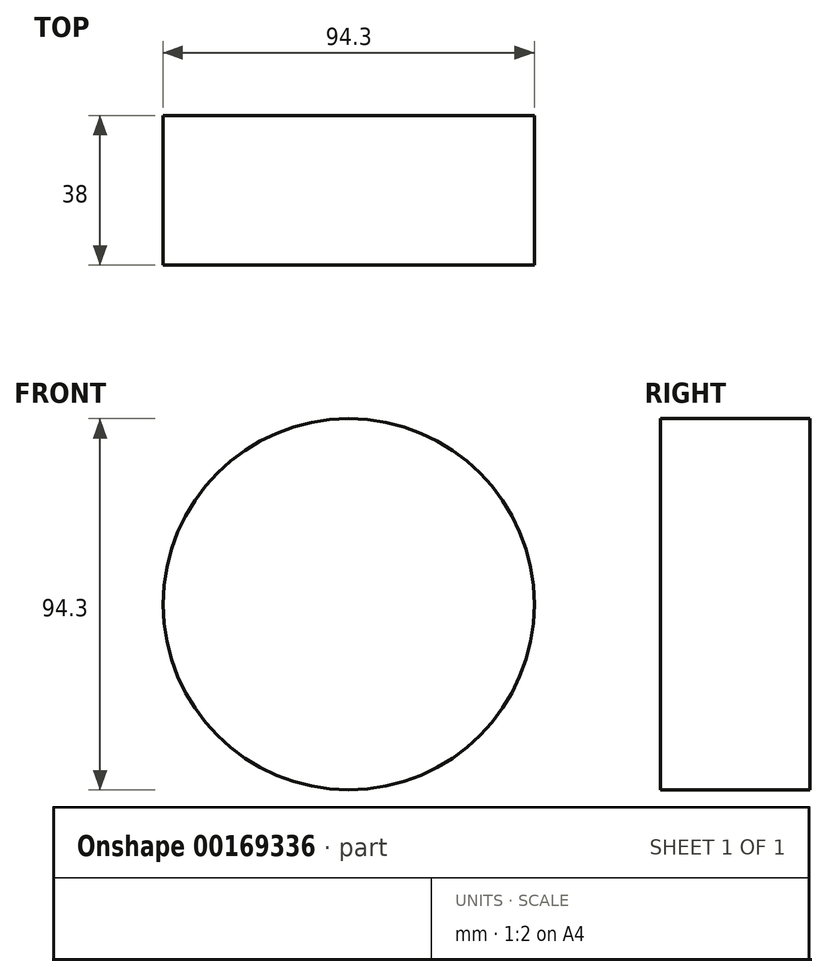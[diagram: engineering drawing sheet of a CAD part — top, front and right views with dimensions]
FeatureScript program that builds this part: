
annotation { "Feature Type Name" : "Feature", "Feature Type Description" : "" }
export const myFeature = defineFeature(function(context is Context, id is Id, definition is map)
    precondition{}
    {
        {
            var Q0;
            Q0=qCreatedBy(makeId("Front.planeOp"),FACE);
            var sketch = newSketch(context, id + "F0", { "sketchPlane" : qUnion([Q0])});
            skCircle(sketch, "E0", {"center": v(0, 0) * mm, "radius": 47.15 * mm});
            skSolve(sketch);
        }
        {
            var Q0;
            Q0=makeQuery(id+"F0.imprint","IMPRINT",FACE,{"disambiguationData":[TD([[makeQuery(id+"F0.imprint","IMPRINT",EDGE,{"derivedFrom":sQuery(id+"F0.wireOp",EDGE,"E0")}),1.0]])]});
            extrude(context, id + "F1", {"entities" : qUnion([Q0]), "depth" : 38 * mm});
        }
    });
